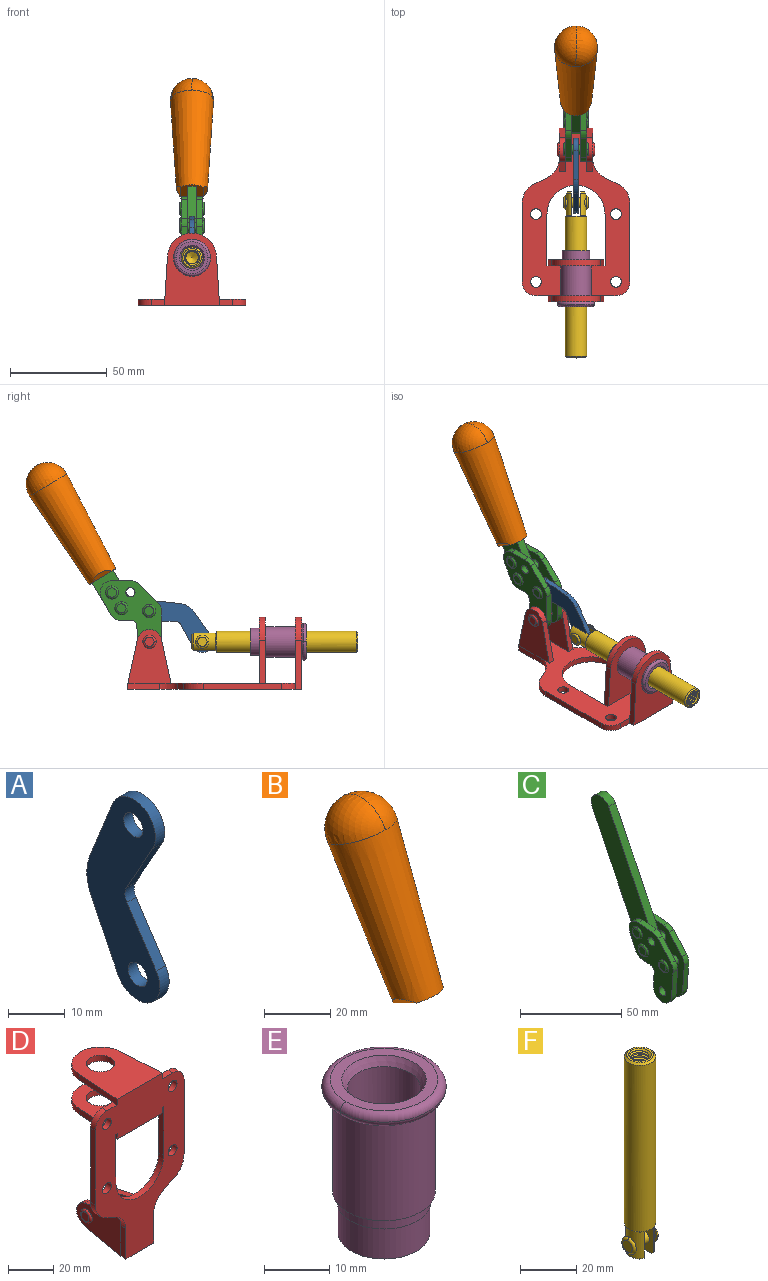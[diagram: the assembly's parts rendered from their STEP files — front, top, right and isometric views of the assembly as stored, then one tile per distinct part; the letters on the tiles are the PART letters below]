
ASSEMBLY  parts=6 mates=6
PART A: 12 faces, bbox 2.3x18.2x42.8 mm
  f0: cylinder r=2.4mm len=4.8mm, axis (1,0,0), area 34.9mm2, adj f4,f11
  f1: cylinder r=10.41mm len=8.47mm, axis (1,0,0), area 20.2mm2, adj f4,f9,f10,f11
  f2: cylinder r=3.05mm len=3.16mm, axis (1,0,0), area 7.7mm2, adj f4,f6,f7,f11
  f3: cylinder r=2.4mm len=4.8mm, axis (1,0,0), area 34.9mm2, adj f4,f11
  f4: plane 42.81x18.23mm, normal (-1,0,0), area 414.1mm2, adj f0,f1,f2,f3,f5,f6,f7,f8
  f5: cylinder r=5.54mm len=10.67mm, axis (1,0,0), area 41.8mm2, adj f4,f6,f10,f11
  f6: plane 11.66x6.53mm, normal (0,-0.87,-0.49), area 30.9mm2, adj f2,f4,f5,f11
  f7: plane 11.17x7.33mm, normal (0,-0.84,0.55), area 30.9mm2, adj f2,f4,f8,f11
  f8: cylinder r=5.54mm len=10.51mm, axis (1,0,0), area 41.8mm2, adj f4,f7,f9,f11
  f9: plane 13.67x6.67mm, normal (0,0.9,-0.44), area 35.1mm2, adj f1,f4,f8,f11
  f10: plane 14.1x5.7mm, normal (0,0.93,0.37), area 35.1mm2, adj f1,f4,f5,f11
  f11: plane 42.81x18.23mm, normal (1,0,0), area 414.1mm2, adj f0,f1,f2,f3,f5,f6,f7,f8
PART B: 11 faces, bbox 22.3x42.6x64.5 mm
  f0: sphere r=11.13mm, area 411.4mm2, adj f1,f8
  f1: cone r=11.11mm half-angle=3.3deg, axis (0,0.44,0.9), area 3251.8mm2, adj f0,f7,f8,f9,f10
  f2: cylinder r=6.16mm len=11.7mm, axis (1,0,0), area 89.5mm2, adj f3,f4,f5,f6
  f3: plane 60.23x36.75mm, normal (-1,0,0), area 763.6mm2, adj f2,f4,f6,f10
  f4: plane 51.37x25.05mm, normal (0,0.9,-0.44), area 264.2mm2, adj f2,f3,f5,f10
  f5: plane 60.23x36.75mm, normal (1,0,0), area 763.6mm2, adj f2,f4,f6,f10
  f6: plane 51.37x25.05mm, normal (0,-0.9,0.44), area 264.2mm2, adj f2,f3,f5,f10
  f7: plane 9.95x5.95mm, normal (0.71,-0.31,-0.64), area 25.8mm2, adj f1,f10
  f8: sphere r=11.13mm, area 411.4mm2, adj f0,f1
  f9: plane 9.95x5.95mm, normal (-0.71,-0.31,-0.64), area 25.8mm2, adj f1,f10
  f10: plane 14.27x11.38mm, normal (0,-0.44,-0.9), area 106.7mm2, adj f1,f3,f4,f5,f6,f7,f9
PART C: 59 faces, bbox 12.9x60.2x99.6 mm
  f0: torus R=2.39mm, axis (-1,0,0), area 14.9mm2, adj f20,f43,f51
  f1: torus R=2.39mm, axis (-1,0,0), area 14.9mm2, adj f19,f42,f51
  f2: torus R=2.39mm, axis (-1,0,0), area 14.9mm2, adj f18,f35,f51
  f3: torus R=2.39mm, axis (-1,0,0), area 14.9mm2, adj f14,f17,f23
  f4: torus R=2.39mm, axis (-1,0,0), area 14.9mm2, adj f13,f16,f23
  f5: torus R=2.39mm, axis (-1,0,0), area 14.9mm2, adj f12,f15,f23
  f6: cylinder r=2.39mm len=4.78mm, axis (1,0,0), area 46.5mm2, adj f48,f50,f51
  f7: cylinder r=2.39mm len=4.78mm, axis (1,0,0), area 46.5mm2, adj f50,f51
  f8: cylinder r=6.35mm len=12.68mm, axis (1,0,0), area 61.8mm2, adj f38,f39,f50,f51
  f9: cylinder r=2.39mm len=4.78mm, axis (-1,0,0), area 70.5mm2, adj f46,f50
  f10: cylinder r=2.39mm len=4.78mm, axis (-1,0,0), area 46.5mm2, adj f23,f45,f46
  f11: cylinder r=2.39mm len=4.78mm, axis (-1,0,0), area 46.5mm2, adj f23,f46
  f12: plane 4.78x4.78mm, normal (1,0,0), area 17.9mm2, adj f5,f15
  f13: plane 4.78x4.78mm, normal (1,0,0), area 17.9mm2, adj f4,f16
  f14: plane 4.78x4.78mm, normal (1,0,0), area 17.9mm2, adj f3,f17
  f15: torus R=2.39mm, axis (-1,0,0), area 14.9mm2, adj f5,f12,f23
  f16: torus R=2.39mm, axis (-1,0,0), area 14.9mm2, adj f4,f13,f23
  f17: torus R=2.39mm, axis (-1,0,0), area 14.9mm2, adj f3,f14,f23
  f18: plane 4.78x4.78mm, normal (-1,0,0), area 17.9mm2, adj f2,f35
  f19: plane 4.78x4.78mm, normal (-1,0,0), area 17.9mm2, adj f1,f42
  f20: plane 4.78x4.78mm, normal (-1,0,0), area 17.9mm2, adj f0,f43
  f21: plane 2.26x0.2mm, normal (1,0,0), area 0.2mm2, adj f31,f44
  f22: plane 2.26x0.2mm, normal (-1,0,0), area 0.2mm2, adj f41,f44
  f23: plane 39.37x30.77mm, normal (1,0,0), area 565.5mm2, adj f3,f4,f5,f10,f11,f15,f16,f17
  f24: cylinder r=6.1mm len=4.15mm, axis (-1,0,0), area 14.7mm2, adj f23,f25,f32,f46
  f25: plane 10.25x9.01mm, normal (0,-0.75,0.66), area 42.3mm2, adj f23,f24,f26,f46
  f26: cylinder r=6.35mm len=4.64mm, axis (-1,0,0), area 15.6mm2, adj f23,f25,f27,f46
  f27: plane 15.84x3.1mm, normal (0,-1,-0.07), area 49.2mm2, adj f23,f26,f28,f46
  f28: cylinder r=6.35mm len=12.68mm, axis (-1,0,0), area 61.8mm2, adj f23,f27,f29,f46
  f29: plane 8.11x3.1mm, normal (0,1,0.07), area 25.2mm2, adj f23,f28,f30,f46
  f30: cylinder r=3.05mm len=3.25mm, axis (-1,0,0), area 14.8mm2, adj f23,f29,f31,f46
  f31: plane 5.99x3.1mm, normal (0,0.07,-1), area 18.6mm2, adj f21,f23,f30,f44,f46
  f32: plane 9.5x3.1mm, normal (0,-0.07,1), area 29.5mm2, adj f23,f24,f33,f46,f47
  f33: cylinder r=6.1mm len=8.63mm, axis (-1,0,0), area 39.1mm2, adj f23,f32,f34,f47
  f34: plane 8.65x3.96mm, normal (0,0.91,-0.42), area 29.5mm2, adj f23,f33,f44,f47
  f35: torus R=2.39mm, axis (-1,0,0), area 14.9mm2, adj f2,f18,f51
  f36: plane 10.25x9.01mm, normal (0,-0.75,0.66), area 42.3mm2, adj f37,f49,f50,f51
  f37: cylinder r=6.35mm len=4.64mm, axis (1,0,0), area 15.6mm2, adj f36,f38,f50,f51
  f38: plane 15.84x3.1mm, normal (0,-1,-0.07), area 49.2mm2, adj f8,f37,f50,f51
  f39: plane 8.11x3.1mm, normal (0,1,0.07), area 25.2mm2, adj f8,f40,f50,f51
  f40: cylinder r=3.05mm len=3.25mm, axis (1,0,0), area 14.8mm2, adj f39,f41,f50,f51
  f41: plane 5.99x3.1mm, normal (0,0.07,-1), area 18.6mm2, adj f22,f40,f44,f50,f51
  f42: torus R=2.39mm, axis (-1,0,0), area 14.9mm2, adj f1,f19,f51
  f43: torus R=2.39mm, axis (-1,0,0), area 14.9mm2, adj f0,f20,f51
  f44: cylinder r=6.35mm len=12.12mm, axis (-1,0,0), area 128.9mm2, adj f21,f22,f23,f31,f34,f41,f46,f47
  f45: plane 2.65x1.35mm, normal (1,0,0), area 1mm2, adj f10,f55
  f46: plane 39.08x20.42mm, normal (-1,0,0), area 412.5mm2, adj f9,f10,f11,f24,f25,f26,f27,f28
  f47: plane 77.62x39.82mm, normal (1,0,0), area 850mm2, adj f32,f33,f34,f44,f53,f54,f55
  f48: plane 2.65x1.35mm, normal (-1,0,0), area 1mm2, adj f6,f55
  f49: cylinder r=6.1mm len=4.15mm, axis (1,0,0), area 14.7mm2, adj f36,f50,f51,f56
  f50: plane 39.08x20.42mm, normal (1,0,0), area 412.5mm2, adj f6,f7,f8,f9,f36,f37,f38,f39
  f51: plane 39.37x30.77mm, normal (-1,0,0), area 565.5mm2, adj f0,f1,f2,f6,f7,f8,f35,f36
  f52: plane 8.65x3.96mm, normal (0,0.91,-0.42), area 29.5mm2, adj f44,f51,f57,f58
  f53: plane 68.49x33.4mm, normal (0,0.9,-0.44), area 358.1mm2, adj f44,f47,f54,f58
  f54: cylinder r=6.35mm len=12.06mm, axis (1,0,0), area 93.7mm2, adj f47,f53,f55,f58
  f55: plane 68.49x33.4mm, normal (0,-0.9,0.44), area 358.1mm2, adj f44,f45,f46,f47,f48,f50,f54,f58
  f56: plane 9.5x3.1mm, normal (0,-0.07,1), area 29.5mm2, adj f49,f50,f51,f57,f58
  f57: cylinder r=6.1mm len=8.63mm, axis (1,0,0), area 39.1mm2, adj f51,f52,f56,f58
  f58: plane 77.62x39.82mm, normal (-1,0,0), area 850mm2, adj f44,f52,f53,f54,f55,f56,f57
PART D: 55 faces, bbox 55.7x37.4x89.8 mm
  f0: torus R=2.41mm, axis (-1,0,0), area 15mm2, adj f11,f15,f25
  f1: torus R=2.41mm, axis (-1,0,0), area 15mm2, adj f10,f12,f22
  f2: cylinder r=2.78mm len=5.56mm, axis (0,-1,0), area 54.2mm2, adj f30,f54
  f3: cylinder r=14.99mm len=29.97mm, axis (0,-1,0), area 145.9mm2, adj f30,f49,f53,f54
  f4: cylinder r=2.78mm len=5.56mm, axis (0,-1,0), area 54.2mm2, adj f30,f54
  f5: cylinder r=2.78mm len=5.56mm, axis (0,-1,0), area 54.2mm2, adj f30,f54
  f6: cylinder r=2.78mm len=5.56mm, axis (0,-1,0), area 54.2mm2, adj f30,f54
  f7: cylinder r=6.35mm len=12.7mm, axis (0,0,1), area 123.6mm2, adj f27,f51
  f8: cylinder r=6.35mm len=12.7mm, axis (0,0,-1), area 124.7mm2, adj f21,f35
  f9: cylinder r=2.41mm len=11.18mm, axis (-1,0,0), area 169.4mm2, adj f16,f19
  f10: plane 4.83x4.83mm, normal (1,0,0), area 18.3mm2, adj f1,f12
  f11: plane 4.83x4.83mm, normal (-1,0,0), area 18.3mm2, adj f0,f15
  f12: torus R=2.41mm, axis (-1,0,0), area 15mm2, adj f1,f10,f22
  f13: cylinder r=6.35mm len=12.41mm, axis (1,0,0), area 53.4mm2, adj f18,f19,f22,f23
  f14: cylinder r=6.35mm len=12.41mm, axis (-1,0,0), area 53.4mm2, adj f16,f17,f24,f25
  f15: torus R=2.41mm, axis (-1,0,0), area 15mm2, adj f0,f11,f25
  f16: plane 27.86x22.35mm, normal (1,0,0), area 425.4mm2, adj f9,f14,f17,f24,f30
  f17: plane 22.86x4.97mm, normal (0,0.21,0.98), area 72.5mm2, adj f14,f16,f25,f30
  f18: plane 22.86x4.97mm, normal (0,0.21,0.98), area 72.5mm2, adj f13,f19,f22,f30
  f19: plane 27.86x22.35mm, normal (-1,0,0), area 425.4mm2, adj f9,f13,f18,f23,f30
  f20: cylinder r=12.7mm len=25.35mm, axis (0,0,-1), area 119.8mm2, adj f21,f34,f35,f36
  f21: plane 34.21x28.07mm, normal (0,0,-1), area 702.4mm2, adj f8,f20,f30,f34,f36
  f22: plane 27.96x22.45mm, normal (1,0,0), area 407.2mm2, adj f1,f12,f13,f18,f23,f30,f42,f43
  f23: plane 22.86x4.97mm, normal (0,0.21,-0.98), area 72.5mm2, adj f13,f19,f22,f44
  f24: plane 22.86x4.97mm, normal (0,0.21,-0.98), area 72.5mm2, adj f14,f16,f25,f44
  f25: plane 27.86x22.35mm, normal (-1,0,0), area 407.1mm2, adj f0,f14,f15,f17,f24,f30,f45,f46
  f26: plane 3.1x0.95mm, normal (0,0,-1), area 2.7mm2, adj f30,f49,f50,f54
  f27: plane 34.21x28.07mm, normal (0,0,1), area 702.4mm2, adj f7,f28,f30,f50,f52
  f28: cylinder r=12.7mm len=25.35mm, axis (0,0,1), area 118.8mm2, adj f27,f50,f51,f52
  f29: plane 3.1x0.95mm, normal (0,0,-1), area 2.7mm2, adj f30,f52,f53,f54
  f30: plane 86.54x55.63mm, normal (0,1,0), area 2362.9mm2, adj f2,f3,f4,f5,f6,f16,f17,f18
  f31: plane 40.56x3.1mm, normal (-1,0,0), area 125.7mm2, adj f30,f32,f48,f54
  f32: cylinder r=7.11mm len=7.11mm, axis (0,-1,0), area 34.6mm2, adj f30,f31,f33,f54
  f33: plane 6.67x3.1mm, normal (0,0,1), area 20.4mm2, adj f30,f32,f34,f54
  f34: plane 25.39x3.13mm, normal (-1,0.06,0), area 79.5mm2, adj f20,f21,f33,f35,f54
  f35: plane 37.31x28.45mm, normal (0,0,1), area 789.9mm2, adj f8,f20,f34,f36,f54
  f36: plane 25.39x3.13mm, normal (1,0.06,0), area 79.5mm2, adj f20,f21,f35,f37,f54
  f37: plane 6.67x3.1mm, normal (0,0,1), area 20.4mm2, adj f30,f36,f38,f54
  f38: cylinder r=7.11mm len=7.11mm, axis (0,-1,0), area 34.6mm2, adj f30,f37,f39,f54
  f39: plane 40.56x3.1mm, normal (1,0,0), area 125.7mm2, adj f30,f38,f40,f54
  f40: cylinder r=11.18mm len=10.16mm, axis (0,-1,0), area 39.5mm2, adj f30,f39,f41,f54
  f41: plane 6.09x3.1mm, normal (0.42,0,-0.91), area 20.8mm2, adj f30,f40,f42,f54
  f42: cylinder r=11.18mm len=9.41mm, axis (0,-1,0), area 37.2mm2, adj f22,f30,f41,f43,f54
  f43: plane 16.5x3.1mm, normal (1,0,0), area 51.1mm2, adj f22,f42,f44,f54
  f44: plane 17.37x3.1mm, normal (0,0,-1), area 53.8mm2, adj f23,f24,f30,f43,f45,f54
  f45: plane 16.5x3.1mm, normal (-1,0,0), area 51.1mm2, adj f25,f44,f46,f54
  f46: cylinder r=11.18mm len=9.41mm, axis (0,-1,0), area 37.2mm2, adj f25,f30,f45,f47,f54
  f47: plane 6.09x3.1mm, normal (-0.42,0,-0.91), area 20.8mm2, adj f30,f46,f48,f54
  f48: cylinder r=11.18mm len=10.16mm, axis (0,-1,0), area 39.5mm2, adj f30,f31,f47,f54
  f49: plane 26.54x3.1mm, normal (-1,0,0), area 82.3mm2, adj f3,f26,f30,f54
  f50: plane 25.39x3.1mm, normal (1,0.06,0), area 78.8mm2, adj f26,f27,f28,f51,f54
  f51: plane 37.31x28.45mm, normal (0,0,-1), area 789.9mm2, adj f7,f28,f50,f52,f54
  f52: plane 25.39x3.1mm, normal (-1,0.06,0), area 78.8mm2, adj f27,f28,f29,f51,f54
  f53: plane 26.54x3.1mm, normal (1,0,0), area 82.3mm2, adj f3,f29,f30,f54
  f54: plane 89.66x55.63mm, normal (0,-1,0), area 2678.5mm2, adj f2,f3,f4,f5,f6,f26,f29,f31
PART E: 15 faces, bbox 20.6x20.6x28.7 mm
  f0: torus R=8.26mm, axis (0,0,1), area 56.8mm2, adj f1,f10,f12
  f1: torus R=8.26mm, axis (0,0,1), area 56.8mm2, adj f0,f6,f13
  f2: cylinder r=5.59mm len=25.91mm, axis (0,0,1), area 909.6mm2, adj f3,f4
  f3: cone r=6.86mm half-angle=45deg, axis (0,0,-1), area 70.2mm2, adj f2,f14
  f4: cone r=6.47mm half-angle=30deg, axis (0,0,1), area 66.7mm2, adj f2,f13
  f5: cylinder r=7.04mm len=14.07mm, axis (0,0,1), area 252.6mm2, adj f11,f14
  f6: torus R=8.26mm, axis (0,0,1), area 56.8mm2, adj f1,f12,f13
  f7: cylinder r=7.16mm len=14.33mm, axis (0,0,1), area 91.5mm2, adj f9,f11
  f8: cylinder r=7.86mm len=18.42mm, axis (0,0,1), area 909.6mm2, adj f9,f10
  f9: plane 15.72x15.72mm, normal (0,0,-1), area 33mm2, adj f7,f8
  f10: plane 16.51x16.51mm, normal (0,0,-1), area 19.9mm2, adj f0,f8,f12
  f11: plane 14.33x14.33mm, normal (0,0,-1), area 5.7mm2, adj f5,f7
  f12: torus R=8.26mm, axis (0,0,1), area 56.8mm2, adj f0,f6,f10
  f13: plane 16.51x16.51mm, normal (0,0,1), area 82.7mm2, adj f1,f4,f6
  f14: plane 14.07x14.07mm, normal (0,0,-1), area 7.8mm2, adj f3,f5
PART F: 48 faces, bbox 12.6x11.1x86.1 mm
  f0: torus R=2.41mm, axis (-1,0,0), area 15mm2, adj f30,f32,f34
  f1: torus R=2.41mm, axis (-1,0,0), area 15mm2, adj f29,f31,f33
  f2: cylinder r=5.54mm len=72.39mm, axis (0,0,1), area 2518.5mm2, adj f3,f4,f42,f43
  f3: cone r=5.54mm half-angle=45deg, axis (0,0,1), area 7.6mm2, adj f2,f5,f41
  f4: cone r=5.54mm half-angle=45deg, axis (0,0,-1), area 34.9mm2, adj f2,f39
  f5: cylinder r=5.08mm len=11.48mm, axis (0,0,1), area 108.3mm2, adj f3,f7,f8,f41
  f6: cylinder r=2.41mm len=4.83mm, axis (-1,0,0), area 71.2mm2, adj f40,f41
  f7: cylinder r=2.41mm len=4.83mm, axis (-1,0,0), area 7.6mm2, adj f5,f34
  f8: cone r=5.08mm half-angle=45deg, axis (0,0,1), area 10.6mm2, adj f5,f37,f41
  f9: cone r=3.98mm half-angle=45deg, axis (0,0,1), area 17.6mm2, adj f27,f39,f45,f46,f47
  f10: cylinder r=2.41mm len=4.83mm, axis (-1,0,0), area 7.6mm2, adj f33,f38
  f11: cylinder r=3.2mm len=6.4mm, axis (0,0,1), area 78.4mm2, adj f12,f28,f44,f45,f47
  f12: cylinder r=3.2mm len=6.4mm, axis (0,0,1), area 10.5mm2, adj f11,f13,f45,f47
  f13: cylinder r=3.2mm len=6.4mm, axis (0,0,1), area 10.5mm2, adj f12,f14,f45,f47
  f14: cylinder r=3.2mm len=6.4mm, axis (0,0,1), area 10.5mm2, adj f13,f15,f45,f47
  f15: cylinder r=3.2mm len=6.4mm, axis (0,0,1), area 10.5mm2, adj f14,f16,f45,f47
  f16: cylinder r=3.2mm len=6.4mm, axis (0,0,1), area 10.5mm2, adj f15,f17,f45,f47
  f17: cylinder r=3.2mm len=6.4mm, axis (0,0,1), area 10.5mm2, adj f16,f18,f45,f47
  f18: cylinder r=3.2mm len=6.4mm, axis (0,0,1), area 10.5mm2, adj f17,f19,f45,f47
  f19: cylinder r=3.2mm len=6.4mm, axis (0,0,1), area 10.5mm2, adj f18,f20,f45,f47
  f20: cylinder r=3.2mm len=6.4mm, axis (0,0,1), area 10.5mm2, adj f19,f21,f45,f47
  f21: cylinder r=3.2mm len=6.4mm, axis (0,0,1), area 10.5mm2, adj f20,f22,f45,f47
  f22: cylinder r=3.2mm len=6.4mm, axis (0,0,1), area 10.5mm2, adj f21,f23,f45,f47
  f23: cylinder r=3.2mm len=6.4mm, axis (0,0,1), area 10.5mm2, adj f22,f24,f45,f47
  f24: cylinder r=3.2mm len=6.4mm, axis (0,0,1), area 10.5mm2, adj f23,f25,f45,f47
  f25: cylinder r=3.2mm len=6.4mm, axis (0,0,1), area 10.5mm2, adj f24,f26,f45,f47
  f26: cylinder r=3.2mm len=6.4mm, axis (0,0,1), area 10.5mm2, adj f25,f27,f45,f47
  f27: cylinder r=3.2mm len=6.4mm, axis (0,0,1), area 7.4mm2, adj f9,f26,f45,f47
  f28: cone r=3.2mm half-angle=60deg, axis (0,0,1), area 37.2mm2, adj f11
  f29: plane 4.83x4.83mm, normal (-1,0,0), area 18.3mm2, adj f1,f31
  f30: plane 4.83x4.83mm, normal (1,0,0), area 18.3mm2, adj f0,f32
  f31: torus R=2.41mm, axis (-1,0,0), area 15mm2, adj f1,f29,f33
  f32: torus R=2.41mm, axis (-1,0,0), area 15mm2, adj f0,f30,f34
  f33: plane 6.83x6.83mm, normal (1,0,0), area 18.3mm2, adj f1,f10,f31
  f34: plane 6.83x6.83mm, normal (-1,0,0), area 18.3mm2, adj f0,f7,f32
  f35: cone r=5.08mm half-angle=45deg, axis (0,0,1), area 10.6mm2, adj f36,f38,f40
  f36: plane 7.25x1.97mm, normal (0,0,-1), area 10mm2, adj f35,f40
  f37: plane 7.25x1.97mm, normal (0,0,-1), area 10mm2, adj f8,f41
  f38: cylinder r=5.08mm len=11.48mm, axis (0,0,1), area 108.3mm2, adj f10,f35,f40,f42
  f39: plane 9.55x9.55mm, normal (0,0,1), area 22mm2, adj f4,f9
  f40: plane 12.76x10.09mm, normal (1,0,0), area 95.7mm2, adj f6,f35,f36,f38,f42,f43
  f41: plane 12.76x10.09mm, normal (-1,0,0), area 95.7mm2, adj f3,f5,f6,f8,f37,f43
  f42: cone r=5.54mm half-angle=45deg, axis (0,0,1), area 7.6mm2, adj f2,f38,f40
  f43: plane 11.07x4.7mm, normal (0,0,-1), area 50.4mm2, adj f2,f40,f41
  f44: plane 0.89x0.62mm, normal (-1,0,0), area 0.3mm2, adj f11,f45,f46,f47
  f45: bspline ~24.8x7.63mm, area 266.6mm2, adj f9,f11,f12,f13,f14,f15,f16,f17
  f46: bspline ~24.87x7.63mm, area 73.6mm2, adj f9,f44,f45,f47
  f47: bspline ~24.98x7.63mm, area 272.5mm2, adj f9,f11,f12,f13,f14,f15,f16,f17
PLACE A rot(axis=(1,0,0),122deg) t=(0,40.09,11.94)mm
PLACE B rot(axis=(-1,0,0),4.7deg) t=(0,19.32,58.6)mm
PLACE C rot(axis=(-1,0,0),4.7deg) t=(0,19.32,58.6)mm
PLACE D rot(axis=(1,0,0),90deg) t=(0,9.14,0)mm fixed
PLACE E rot(axis=(1,0,0),90deg) t=(0,9.14,0)mm
PLACE F rot(axis=(1,0,0),90deg) t=(0,29.4,0)mm
MATE revolute A.f5 <-> F.f6  axis (1,0,0) through (0,13.92,24.61)mm
MATE fastened C.f54 <-> B.f2  axis (1,0,0) through (0,94.58,107.41)mm
MATE revolute A.f3 <-> C.f4  axis (1,0,0) through (0,41.42,40.49)mm
MATE revolute D.f0 <-> C.f7  axis (-1,0,0) through (0,41.23,24.61)mm
MATE slider F.f2 <-> D.f7  axis (0,-1,0) through (0,-29.38,24.61)mm
MATE fastened D.f7 <-> E.f0  axis (0,-1,0) through (0,-37.25,24.61)mm
